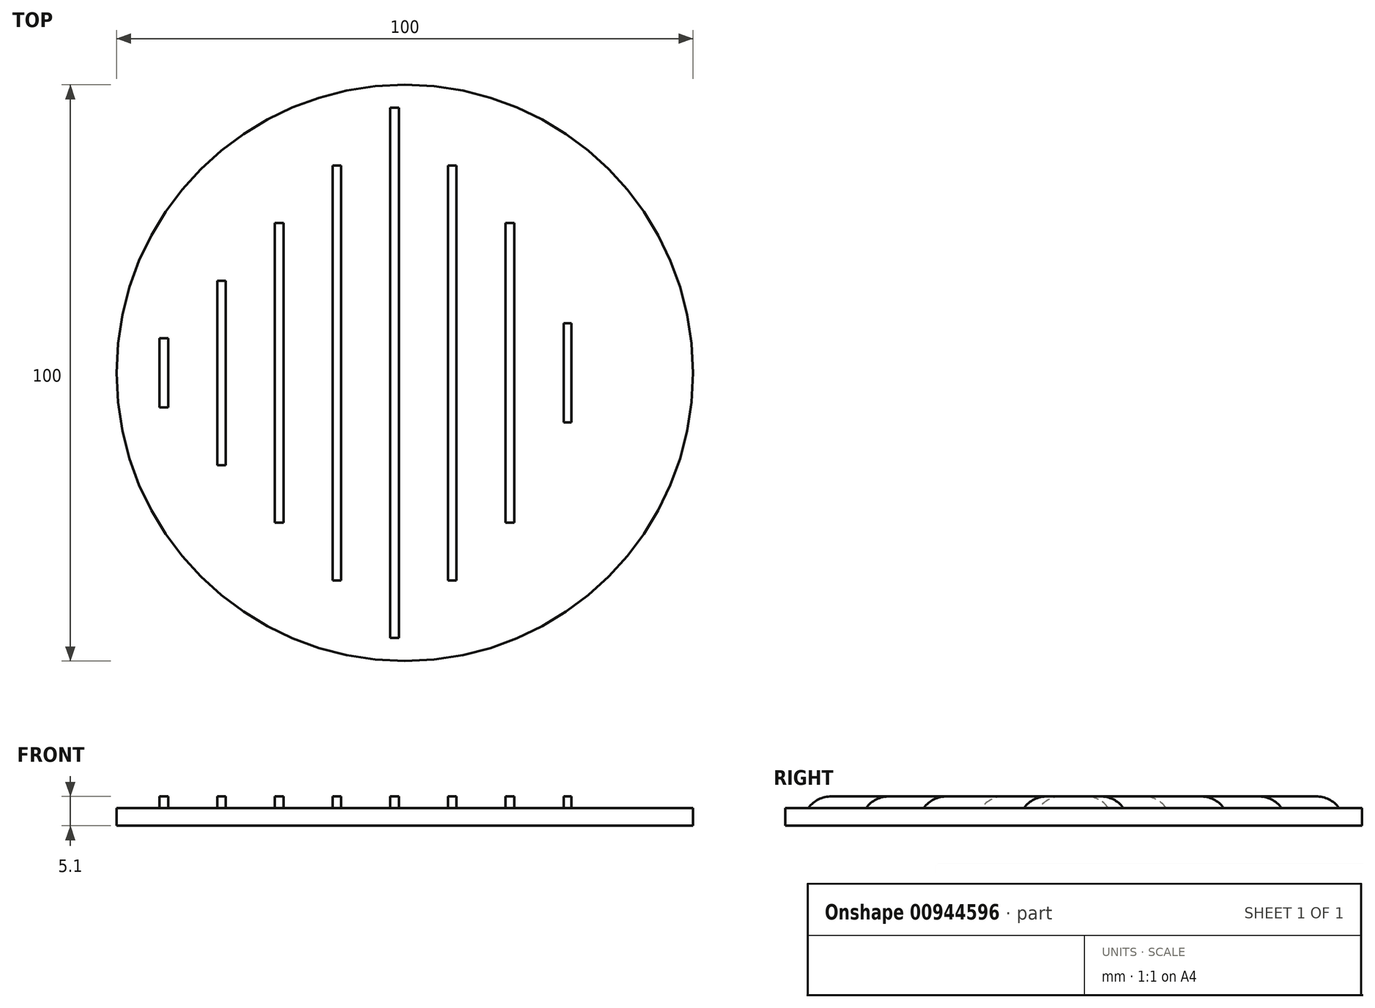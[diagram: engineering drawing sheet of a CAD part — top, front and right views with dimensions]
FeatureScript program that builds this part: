
annotation { "Feature Type Name" : "Feature", "Feature Type Description" : "" }
export const myFeature = defineFeature(function(context is Context, id is Id, definition is map)
    precondition{}
    {
        {
            var Q0;
            Q0=qCreatedBy(makeId("Top.planeOp"),FACE);
            var sketch = newSketch(context, id + "F0", { "sketchPlane" : qUnion([Q0])});
            skCircle(sketch, "E0", {"center": v(1.79, 0) * mm, "radius": 50 * mm});
            skSolve(sketch);
        }
        {
            var Q0;
            Q0 = qSketchRegion(id + "F0", true);
            extrude(context, id + "F1", {"entities" : qUnion([Q0]), "depth" : 3.1 * mm, "offsetDistance" : 25 * mm});
        }
        {
            var Q0;
            Q0=makeQuery(id+"F1.opExtrude","CAP_FACE",FACE,{"disambiguationData":[OSD([sQuery(id+"F0.wireOp",EDGE,"E0")])],"isStart":false});
            var sketch = newSketch(context, id + "F2", { "sketchPlane" : qUnion([Q0])});
            skLineSegment(sketch, "E1.bottom", {"start": v(-0.75, 46) * mm, "end": v(0.75, 46) * mm});
            skLineSegment(sketch, "E1.top", {"start": v(-0.75, -46) * mm, "end": v(0.75, -46) * mm});
            skLineSegment(sketch, "E1.left", {"start": v(-0.75, 46) * mm, "end": v(-0.75, -46) * mm});
            skLineSegment(sketch, "E1.right", {"start": v(0.75, 46) * mm, "end": v(0.75, -46) * mm});
            skPoint(sketch, "E1.middle", {"position": v(0, 0) * mm});
            skLineSegment(sketch, "E2", {"start": v(0, 0) * mm, "end": v(-10, 0) * mm, "construction": true});
            skLineSegment(sketch, "E3", {"start": v(-10, 0) * mm, "end": v(-20, 0) * mm, "construction": true});
            skLineSegment(sketch, "E4", {"start": v(-20, 0) * mm, "end": v(-30, 0) * mm, "construction": true});
            skLineSegment(sketch, "E5", {"start": v(-30, 0) * mm, "end": v(-40, 0) * mm, "construction": true});
            skLineSegment(sketch, "E6", {"start": v(0, 0) * mm, "end": v(10, 0) * mm, "construction": true});
            skLineSegment(sketch, "E7", {"start": v(10, 0) * mm, "end": v(20, 0) * mm, "construction": true});
            skLineSegment(sketch, "E8", {"start": v(20, 0) * mm, "end": v(30, 0) * mm, "construction": true});
            skLineSegment(sketch, "E9", {"start": v(30, 0) * mm, "end": v(40, 0) * mm, "construction": true});
            skLineSegment(sketch, "E10.bottom", {"start": v(-9.25, 36) * mm, "end": v(-10.75, 36) * mm});
            skLineSegment(sketch, "E10.top", {"start": v(-9.25, -36) * mm, "end": v(-10.75, -36) * mm});
            skLineSegment(sketch, "E10.left", {"start": v(-9.25, 36) * mm, "end": v(-9.25, -36) * mm});
            skLineSegment(sketch, "E10.right", {"start": v(-10.75, 36) * mm, "end": v(-10.75, -36) * mm});
            skPoint(sketch, "E10.middle", {"position": v(-10, 0) * mm});
            skLineSegment(sketch, "E11.bottom", {"start": v(-19.25, 26) * mm, "end": v(-20.75, 26) * mm});
            skLineSegment(sketch, "E11.top", {"start": v(-19.25, -26) * mm, "end": v(-20.75, -26) * mm});
            skLineSegment(sketch, "E11.left", {"start": v(-19.25, 26) * mm, "end": v(-19.25, -26) * mm});
            skLineSegment(sketch, "E11.right", {"start": v(-20.75, 26) * mm, "end": v(-20.75, -26) * mm});
            skPoint(sketch, "E11.middle", {"position": v(-20, 0) * mm});
            skLineSegment(sketch, "E12.bottom", {"start": v(-29.25, 16) * mm, "end": v(-30.75, 16) * mm});
            skLineSegment(sketch, "E12.top", {"start": v(-29.25, -16) * mm, "end": v(-30.75, -16) * mm});
            skLineSegment(sketch, "E12.left", {"start": v(-29.25, 16) * mm, "end": v(-29.25, -16) * mm});
            skLineSegment(sketch, "E12.right", {"start": v(-30.75, 16) * mm, "end": v(-30.75, -16) * mm});
            skPoint(sketch, "E12.middle", {"position": v(-30, 0) * mm});
            skLineSegment(sketch, "E13.bottom", {"start": v(-39.25, 6) * mm, "end": v(-40.75, 6) * mm});
            skLineSegment(sketch, "E13.top", {"start": v(-39.25, -6) * mm, "end": v(-40.75, -6) * mm});
            skLineSegment(sketch, "E13.left", {"start": v(-39.25, 6) * mm, "end": v(-39.25, -6) * mm});
            skLineSegment(sketch, "E13.right", {"start": v(-40.75, 6) * mm, "end": v(-40.75, -6) * mm});
            skPoint(sketch, "E13.middle", {"position": v(-40, 0) * mm});
            skLineSegment(sketch, "E14.MirrorCS", {"start": v(-9.25, -36) * mm, "end": v(-9.25, 36) * mm});
            skLineSegment(sketch, "E15.MirrorCS", {"start": v(-10.75, -36) * mm, "end": v(-10.75, 36) * mm});
            skLineSegment(sketch, "E16.bottom", {"start": v(10.75, 36) * mm, "end": v(9.25, 36) * mm});
            skLineSegment(sketch, "E16.top", {"start": v(10.75, -36) * mm, "end": v(9.25, -36) * mm});
            skLineSegment(sketch, "E16.left", {"start": v(10.75, 36) * mm, "end": v(10.75, -36) * mm});
            skLineSegment(sketch, "E16.right", {"start": v(9.25, 36) * mm, "end": v(9.25, -36) * mm});
            skPoint(sketch, "E16.middle", {"position": v(10, 0) * mm});
            skLineSegment(sketch, "E17.bottom", {"start": v(19.25, 26) * mm, "end": v(20.75, 26) * mm});
            skLineSegment(sketch, "E17.top", {"start": v(19.25, -26) * mm, "end": v(20.75, -26) * mm});
            skLineSegment(sketch, "E17.left", {"start": v(19.25, 26) * mm, "end": v(19.25, -26) * mm});
            skLineSegment(sketch, "E17.right", {"start": v(20.75, 26) * mm, "end": v(20.75, -26) * mm});
            skPoint(sketch, "E17.middle", {"position": v(20, 0) * mm});
            skLineSegment(sketch, "E18.bottom", {"start": v(29.32, 8.61) * mm, "end": v(30.68, 8.61) * mm});
            skLineSegment(sketch, "E18.top", {"start": v(29.32, -8.61) * mm, "end": v(30.68, -8.61) * mm});
            skLineSegment(sketch, "E18.left", {"start": v(29.32, 8.61) * mm, "end": v(29.32, -8.61) * mm});
            skLineSegment(sketch, "E18.right", {"start": v(30.68, 8.61) * mm, "end": v(30.68, -8.61) * mm});
            skPoint(sketch, "E18.middle", {"position": v(30, 0) * mm});
            skSolve(sketch);
        }
        {
            var Q0;
            Q0 = qSketchRegion(id + "F2", true);
            extrude(context, id + "F3", {"entities" : qUnion([Q0]), "operationType" : NewBodyOperationType.ADD, "depth" : 2 * mm, "offsetDistance" : 25 * mm});
        }
        {
            var Q0;
            Q0=makeQuery(id+"F3.opExtrude","CAP_EDGE",EDGE,{"disambiguationData":[OSD([sQuery(id+"F2.wireOp",EDGE,"E10.bottom")])],"isStart":false});
            var Q1;
            Q1=makeQuery(id+"F3.opExtrude","CAP_EDGE",EDGE,{"disambiguationData":[OSD([sQuery(id+"F2.wireOp",EDGE,"E11.bottom")])],"isStart":false});
            var Q2;
            Q2=makeQuery(id+"F3.opExtrude","CAP_EDGE",EDGE,{"disambiguationData":[OSD([sQuery(id+"F2.wireOp",EDGE,"E12.bottom")])],"isStart":false});
            var Q3;
            Q3=makeQuery(id+"F3.opExtrude","CAP_EDGE",EDGE,{"disambiguationData":[OSD([sQuery(id+"F2.wireOp",EDGE,"E13.bottom")])],"isStart":false});
            var Q4;
            Q4=makeQuery(id+"F3.opExtrude","CAP_EDGE",EDGE,{"disambiguationData":[OSD([sQuery(id+"F2.wireOp",EDGE,"E13.top")])],"isStart":false});
            var Q5;
            Q5=makeQuery(id+"F3.opExtrude","CAP_EDGE",EDGE,{"disambiguationData":[OSD([sQuery(id+"F2.wireOp",EDGE,"E12.top")])],"isStart":false});
            var Q6;
            Q6=makeQuery(id+"F3.opExtrude","CAP_EDGE",EDGE,{"disambiguationData":[OSD([sQuery(id+"F2.wireOp",EDGE,"E11.top")])],"isStart":false});
            var Q7;
            Q7=makeQuery(id+"F3.opExtrude","CAP_EDGE",EDGE,{"disambiguationData":[OSD([sQuery(id+"F2.wireOp",EDGE,"E10.top")])],"isStart":false});
            var Q8;
            Q8=makeQuery(id+"F3.opExtrude","CAP_EDGE",EDGE,{"disambiguationData":[OSD([sQuery(id+"F2.wireOp",EDGE,"E16.top")])],"isStart":false});
            var Q9;
            Q9=makeQuery(id+"F3.opExtrude","CAP_EDGE",EDGE,{"disambiguationData":[OSD([sQuery(id+"F2.wireOp",EDGE,"E16.bottom")])],"isStart":false});
            var Q10;
            Q10=makeQuery(id+"F3.opExtrude","CAP_EDGE",EDGE,{"disambiguationData":[OSD([sQuery(id+"F2.wireOp",EDGE,"E17.bottom")])],"isStart":false});
            var Q11;
            Q11=makeQuery(id+"F3.opExtrude","CAP_EDGE",EDGE,{"disambiguationData":[OSD([sQuery(id+"F2.wireOp",EDGE,"E17.top")])],"isStart":false});
            var Q12;
            Q12=makeQuery(id+"F3.opExtrude","CAP_EDGE",EDGE,{"disambiguationData":[OSD([sQuery(id+"F2.wireOp",EDGE,"E18.top")])],"isStart":false});
            var Q13;
            Q13=makeQuery(id+"F3.opExtrude","CAP_EDGE",EDGE,{"disambiguationData":[OSD([sQuery(id+"F2.wireOp",EDGE,"E18.bottom")])],"isStart":false});
            var Q14;
            Q14=makeQuery(id+"F3.opExtrude","CAP_EDGE",EDGE,{"disambiguationData":[OSD([sQuery(id+"F2.wireOp",EDGE,"E1.bottom")])],"isStart":false});
            var Q15;
            Q15=makeQuery(id+"F3.opExtrude","CAP_EDGE",EDGE,{"disambiguationData":[OSD([sQuery(id+"F2.wireOp",EDGE,"E1.top")])],"isStart":false});
            fillet(context, id + "F4", {"entities" : qUnion([Q0, Q1, Q2, Q3, Q4, Q5, Q6, Q7, Q8, Q9, Q10, Q11, Q12, Q13, Q14, Q15]), "radius" : 5 * mm, "tangentPropagation" : true, "allowEdgeOverflow" : false});
        }
    });
